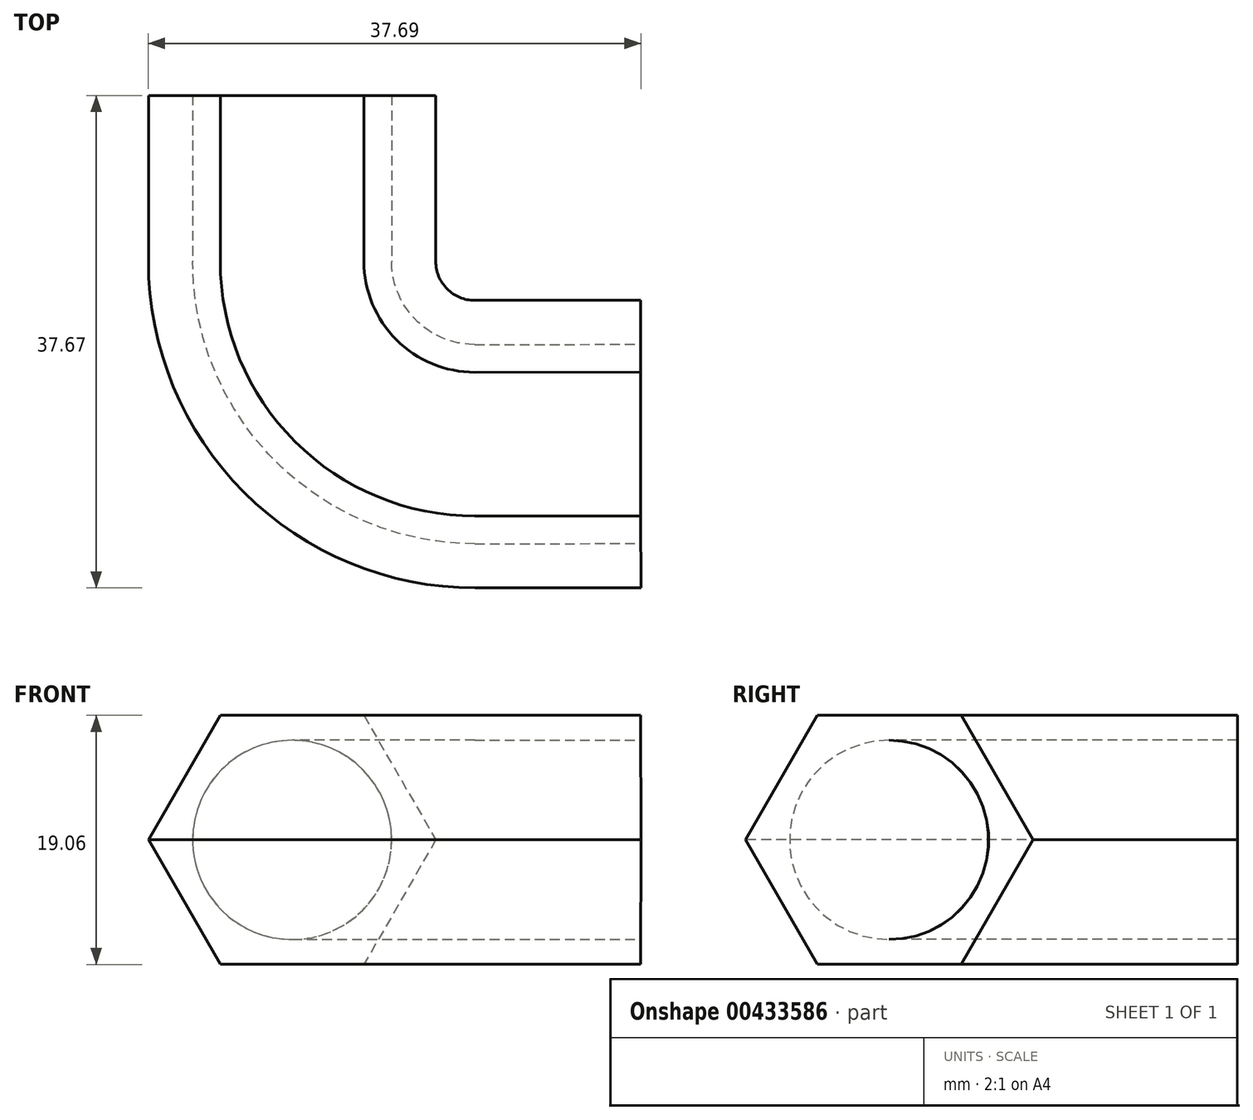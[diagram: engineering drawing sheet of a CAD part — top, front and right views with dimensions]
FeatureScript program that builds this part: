
annotation { "Feature Type Name" : "Feature", "Feature Type Description" : "" }
export const myFeature = defineFeature(function(context is Context, id is Id, definition is map)
    precondition{}
    {
        {
            var Q0;
            Q0=qCreatedBy(makeId("Front.planeOp"),FACE);
            var sketch = newSketch(context, id + "F0", { "sketchPlane" : qUnion([Q0])});
            skCircle(sketch, "E0.cCircle", {"center": v(0, 0) * mm, "radius": 9.53 * mm, "construction": true});
            skLineSegment(sketch, "E0.0", {"start": v(-5.5, 9.53) * mm, "end": v(5.5, 9.53) * mm});
            skLineSegment(sketch, "E0.1", {"start": v(5.5, 9.53) * mm, "end": v(11, 0) * mm});
            skLineSegment(sketch, "E0.2", {"start": v(11, 0) * mm, "end": v(5.5, -9.52) * mm});
            skLineSegment(sketch, "E0.3", {"start": v(5.5, -9.52) * mm, "end": v(-5.5, -9.53) * mm});
            skLineSegment(sketch, "E0.4", {"start": v(-5.5, -9.53) * mm, "end": v(-11, 0) * mm});
            skLineSegment(sketch, "E0.5", {"start": v(-11, 0) * mm, "end": v(-5.5, 9.52) * mm});
            skPoint(sketch, "E0.0.midPoint", {"position": v(0, 9.53) * mm});
            skCircle(sketch, "E1", {"center": v(0, 0) * mm, "radius": 7.62 * mm});
            skSolve(sketch);
        }
        {
            var Q0;
            Q0=qCreatedBy(makeId("Top.planeOp"),FACE);
            var sketch = newSketch(context, id + "F1", { "sketchPlane" : qUnion([Q0])});
            skLineSegment(sketch, "E2", {"start": v(0, 0) * mm, "end": v(0, -12.7) * mm});
            skArc(sketch, "E3", {"start": v(0, -12.7) * mm, "mid": v(4.1, -22.58) * mm, "end": v(13.98, -26.67) * mm});
            skLineSegment(sketch, "E4", {"start": v(13.98, -26.67) * mm, "end": v(26.68, -26.66) * mm});
            skSolve(sketch);
        }
        {
            var Q0;
            Q0=makeQuery(id+"F0.imprint","IMPRINT",FACE,{"disambiguationData":[TD([[makeQuery(id+"F0.imprint","IMPRINT",EDGE,{"derivedFrom":sQuery(id+"F0.wireOp",EDGE,"E0.0")}),-1.0]])]});
            var Q1;
            Q1=qConstructionFilter(qBodyType(qCreatedBy(id+"F1",EDGE),BodyType.WIRE),ConstructionObject.NO);
            sweep(context, id + "F2", {"profiles" : qUnion([Q0]), "path" : qUnion([Q1])});
        }
    });
